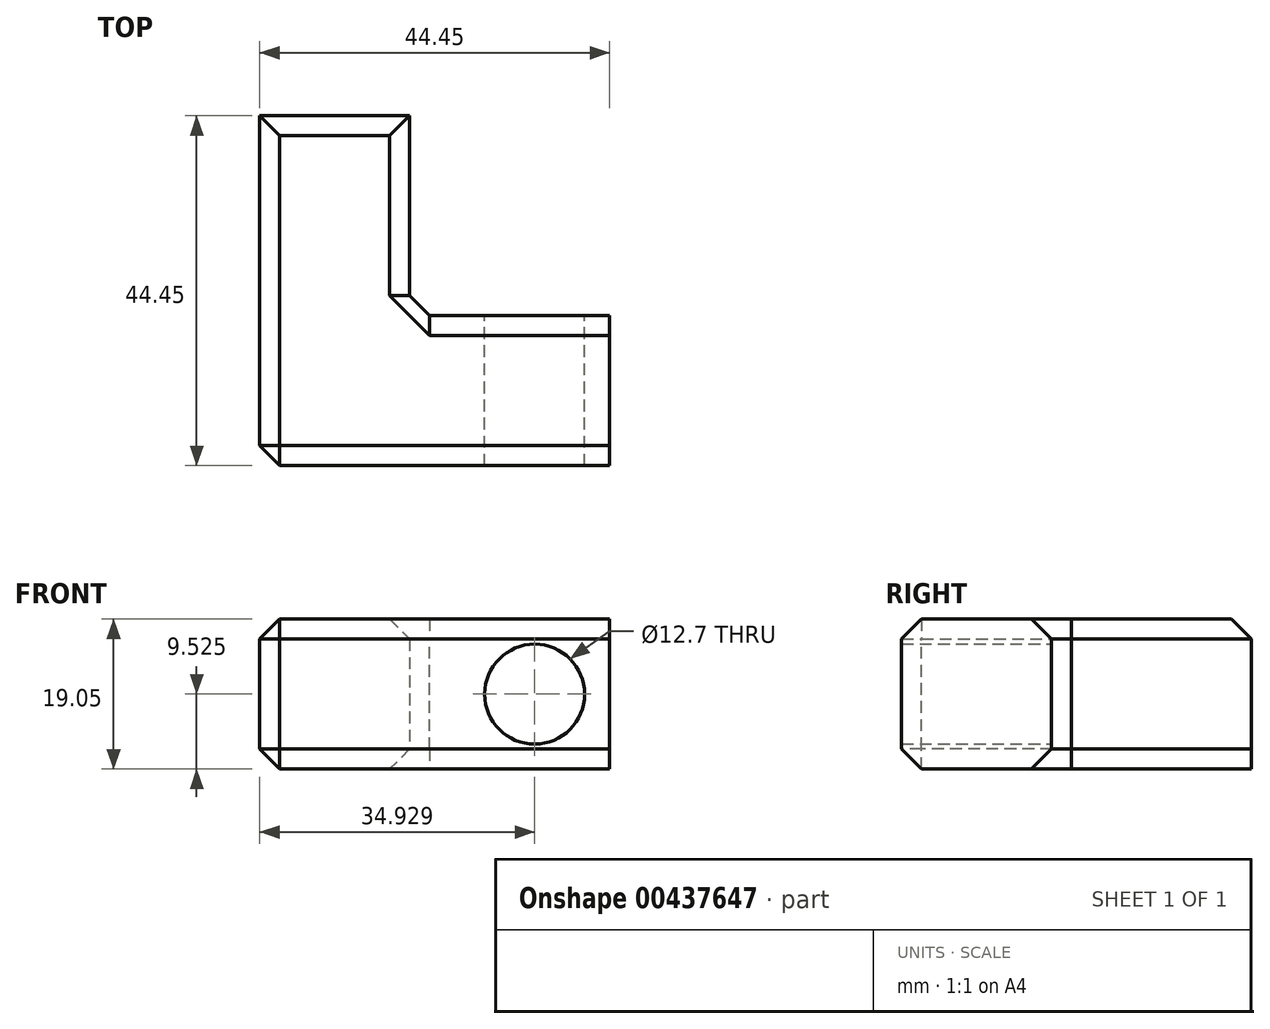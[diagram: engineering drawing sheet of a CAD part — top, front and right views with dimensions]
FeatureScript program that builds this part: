
annotation { "Feature Type Name" : "Feature", "Feature Type Description" : "" }
export const myFeature = defineFeature(function(context is Context, id is Id, definition is map)
    precondition{}
    {
        {
            var Q0;
            Q0=qCreatedBy(makeId("Top.planeOp"),FACE);
            var sketch = newSketch(context, id + "F0", { "sketchPlane" : qUnion([Q0])});
            skLineSegment(sketch, "E0.bottom", {"start": v(-38.34, 35.7) * mm, "end": v(-19.29, 35.7) * mm});
            skLineSegment(sketch, "E0.top", {"start": v(-38.34, -8.75) * mm, "end": v(6.11, -8.75) * mm});
            skLineSegment(sketch, "E0.left", {"start": v(-38.34, 35.7) * mm, "end": v(-38.34, -8.75) * mm});
            skLineSegment(sketch, "E0.right", {"start": v(-19.29, 35.7) * mm, "end": v(-19.29, 10.3) * mm});
            skLineSegment(sketch, "E1.top", {"start": v(-19.29, 10.3) * mm, "end": v(6.11, 10.3) * mm});
            skLineSegment(sketch, "E1.right", {"start": v(6.11, -8.75) * mm, "end": v(6.11, 10.3) * mm});
            skSolve(sketch);
        }
        {
            var Q0;
            Q0=qSketchRegion(id+"F0",true);
            extrude(context, id + "F1", {"entities" : qUnion([Q0]), "depth" : 19.05 * mm});
        }
        {
            var Q0;
            Q0=makeQuery(id+"F1.opExtrude","SWEPT_EDGE",EDGE,{"disambiguationData":[OSD([sQuery(id+"F0.wireOp",EDGE,"E0.right"),sQuery(id+"F0.wireOp",EDGE,"E1.top")])]});
            var Q1;
            Q1=makeQuery(id+"F1.opExtrude","CAP_EDGE",EDGE,{"disambiguationData":[OSD([sQuery(id+"F0.wireOp",EDGE,"E0.bottom")])],"isStart":false});
            var Q2;
            Q2=makeQuery(id+"F1.opExtrude","CAP_EDGE",EDGE,{"disambiguationData":[OSD([sQuery(id+"F0.wireOp",EDGE,"E0.left")])],"isStart":false});
            var Q3;
            Q3=makeQuery(id+"F1.opExtrude","CAP_EDGE",EDGE,{"disambiguationData":[OSD([sQuery(id+"F0.wireOp",EDGE,"E0.top")])],"isStart":false});
            var Q4;
            Q4=makeQuery(id+"F1.opExtrude","CAP_EDGE",EDGE,{"disambiguationData":[OSD([sQuery(id+"F0.wireOp",EDGE,"E0.left")])],"isStart":true});
            var Q5;
            Q5=makeQuery(id+"F1.opExtrude","SWEPT_EDGE",EDGE,{"disambiguationData":[OSD([sQuery(id+"F0.wireOp",EDGE,"E0.top"),sQuery(id+"F0.wireOp",EDGE,"E0.left")])]});
            var Q6;
            Q6=makeQuery(id+"F1.opExtrude","CAP_EDGE",EDGE,{"disambiguationData":[OSD([sQuery(id+"F0.wireOp",EDGE,"E0.top")])],"isStart":true});
            var Q7;
            Q7=makeQuery(id+"F1.opExtrude","CAP_EDGE",EDGE,{"disambiguationData":[OSD([sQuery(id+"F0.wireOp",EDGE,"E1.top")])],"isStart":true});
            var Q8;
            Q8=makeQuery(id+"F1.opExtrude","CAP_EDGE",EDGE,{"disambiguationData":[OSD([sQuery(id+"F0.wireOp",EDGE,"E1.top")])],"isStart":false});
            chamfer(context, id + "F2", {"entities" : qUnion([Q0, Q1, Q2, Q3, Q4, Q5, Q6, Q7, Q8]), "width" : 2.54 * mm, "tangentPropagation" : true});
        }
        {
            var Q0;
            Q0=makeQuery(id+"F1.opExtrude","SWEPT_FACE",FACE,{"disambiguationData":[OSD([sQuery(id+"F0.wireOp",EDGE,"E1.top")])]});
            var sketch = newSketch(context, id + "F3", { "sketchPlane" : qUnion([Q0])});
            skLineSegment(sketch, "E2.bottom", {"start": v(-6.11, 19.05) * mm, "end": v(3.41, 19.05) * mm});
            skLineSegment(sketch, "E2.top", {"start": v(-6.11, 9.53) * mm, "end": v(3.41, 9.53) * mm});
            skLineSegment(sketch, "E2.left", {"start": v(-6.11, 19.05) * mm, "end": v(-6.11, 9.53) * mm});
            skLineSegment(sketch, "E2.right", {"start": v(3.41, 19.05) * mm, "end": v(3.41, 9.53) * mm});
            skSolve(sketch);
        }
        {
            var Q0;
            Q0=sQuery(id+"F3.wireOp",VERTEX,"E2.right.end");
            var Q1;
            Q1=makeQuery(id+"F1.opExtrude","SWEPT_BODY",BODY,{"disambiguationData":[OSD([sQuery(id+"F0.wireOp",EDGE,"E0.bottom"),sQuery(id+"F0.wireOp",EDGE,"E0.top"),sQuery(id+"F0.wireOp",EDGE,"E0.left"),sQuery(id+"F0.wireOp",EDGE,"E0.right"),sQuery(id+"F0.wireOp",EDGE,"E1.top"),sQuery(id+"F0.wireOp",EDGE,"E1.right")])]});
            hole(context, id + "F4", {"style" : HoleStyle.SIMPLE, "endStyle" : HoleEndStyle.THROUGH, "holeDiameter" : 12.7 * mm, "isTappedThrough" : true, "tappedDepth" : 12.7 * mm, "tapClearance" : 3, "startFromSketch" : true, "locations" : qUnion([Q0]), "scope" : qUnion([Q1])});
        }
    });
